# Revit family: ВКО прес_турбо
name_source: partatom
category: Mechanical Equipment
units: mm (PartAtom-declared; Revit-internal decimal feet)

## family parameters
Always vertical = Yes
Classification = None
Cut with Voids When Loaded = No
Part Type = Normal
Room Calculation Point = No
Round Connector Dimension = Use Diameter
Shared = No
Work Plane-Based = No

## types (6) — shared parameters
00_20_Виробник = Вентс
00_20_Назва = Осьовий вентилятор
Manufacturer = Вентс
URL = https://vents.ua
Класифікація навантаження = HVAC
Кількість фаз = 1
Матеріал зони обслуговуваня = <By Category>
Матеріал корпусу = Пластмаса, непрозора, біла
Напруга = 230 V
Частота = 50 Hz
zero-valued in all types: Default Elevation

## per-type parameters (varying)
| type | D | D1 | Dy | L | L1 | R | R1 | Ry | Вага | Довжина | Діаметр | Максимальний потік повітря | Потужність | Рівень звукового тиску на відстані 3 м | Струм | Установлена потужність |
| 100 ВКО прес | 100 mm  [stored 0.328084 ft] | 104 mm | 98 mm  [stored 0.321522 ft] | 91 mm  [stored 0.298556 ft] | 31 mm  [stored 0.101706 ft] | 50 mm  [stored 0.164042 ft] | 52 mm | 49 mm  [stored 0.160761 ft] | 0.41 kg | 91 mm  [stored 0.298556 ft] | 100 mm  [stored 0.328084 ft] | 106.0 m³/h | 16 W | 39 дБА | 0.100 A | 23 W |
| 125 ВКО прес | 125 mm  [stored 0.410105 ft] | 129 mm | 123 mm  [stored 0.403543 ft] | 93 mm  [stored 0.305118 ft] | 31 mm  [stored 0.101706 ft] | 63 mm | 65 mm | 62 mm | 0.48 kg | 93 mm  [stored 0.305118 ft] | 125 mm  [stored 0.410105 ft] | 192.0 m³/h | 24 W | 39 дБА | 0.105 A | 24 W |
| 150 ВКО прес | 150 mm | 154 mm  [stored 0.505249 ft] | 148 mm  [stored 0.485564 ft] | 108 mm  [stored 0.354331 ft] | 46 mm  [stored 0.150919 ft] | 75 mm | 77 mm  [stored 0.252625 ft] | 74 mm  [stored 0.242782 ft] | 0.80 kg | 108 mm  [stored 0.354331 ft] | 150 mm | 312.0 m³/h | 29 W | 44 дБА | 0.130 A | 30 W |
| 100 ВКО турбо | 100 mm  [stored 0.328084 ft] | 104 mm | 98 mm  [stored 0.321522 ft] | 91 mm  [stored 0.298556 ft] | 31 mm  [stored 0.101706 ft] | 50 mm  [stored 0.164042 ft] | 52 mm | 49 mm  [stored 0.160761 ft] | 0.41 kg | 91 mm  [stored 0.298556 ft] | 100 mm  [stored 0.328084 ft] | 135.0 m³/h | 16 W | 38 дБА | 0.100 A | 23 W |
| 125 ВКО турбо | 125 mm  [stored 0.410105 ft] | 129 mm | 123 mm  [stored 0.403543 ft] | 93 mm  [stored 0.305118 ft] | 31 mm  [stored 0.101706 ft] | 63 mm | 65 mm | 62 mm | 0.48 kg | 93 mm  [stored 0.305118 ft] | 125 mm  [stored 0.410105 ft] | 243.0 m³/h | 24 W | 39 дБА | 0.105 A | 24 W |
| 150 ВКО турбо | 150 mm | 154 mm  [stored 0.505249 ft] | 148 mm  [stored 0.485564 ft] | 108 mm  [stored 0.354331 ft] | 46 mm  [stored 0.150919 ft] | 75 mm | 77 mm  [stored 0.252625 ft] | 74 mm  [stored 0.242782 ft] | 0.80 kg | 108 mm  [stored 0.354331 ft] | 150 mm | 358.0 m³/h | 29 W | 44 дБА | 0.130 A | 30 W |

note: column(s) folded — value = type name in every type: 00_20_Тип

note: [stored X ft] marks values corroborated as IEEE doubles in the binary element streams (Revit-internal decimal feet)
